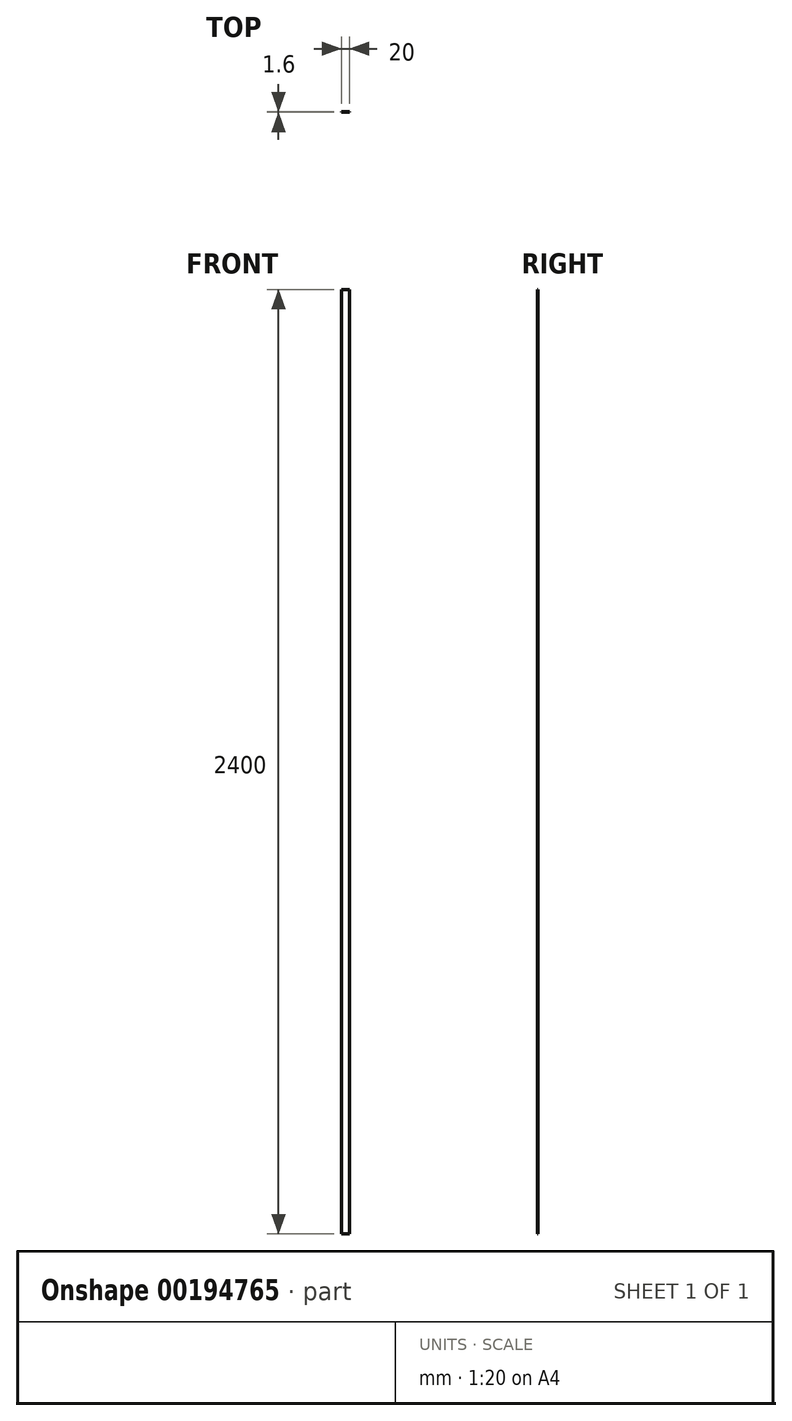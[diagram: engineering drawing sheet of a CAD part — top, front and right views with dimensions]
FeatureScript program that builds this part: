
annotation { "Feature Type Name" : "Feature", "Feature Type Description" : "" }
export const myFeature = defineFeature(function(context is Context, id is Id, definition is map)
    precondition{}
    {
        {
            var Q0;
            Q0=qCreatedBy(makeId("Front.planeOp"),FACE);
            var sketch = newSketch(context, id + "F0", { "sketchPlane" : qUnion([Q0])});
            skLineSegment(sketch, "E0.bottom", {"start": v(10, 1200) * mm, "end": v(-10, 1200) * mm});
            skLineSegment(sketch, "E0.top", {"start": v(10, -1200) * mm, "end": v(-10, -1200) * mm});
            skLineSegment(sketch, "E0.left", {"start": v(10, 1200) * mm, "end": v(10, -1200) * mm});
            skLineSegment(sketch, "E0.right", {"start": v(-10, 1200) * mm, "end": v(-10, -1200) * mm});
            skPoint(sketch, "E0.middle", {"position": v(0, 0) * mm});
            skSolve(sketch);
        }
        {
            var Q0;
            Q0 = qSketchRegion(id + "F0", true);
            extrude(context, id + "F1", {"entities" : qUnion([Q0]), "depth" : 1.6 * mm});
        }
    });
